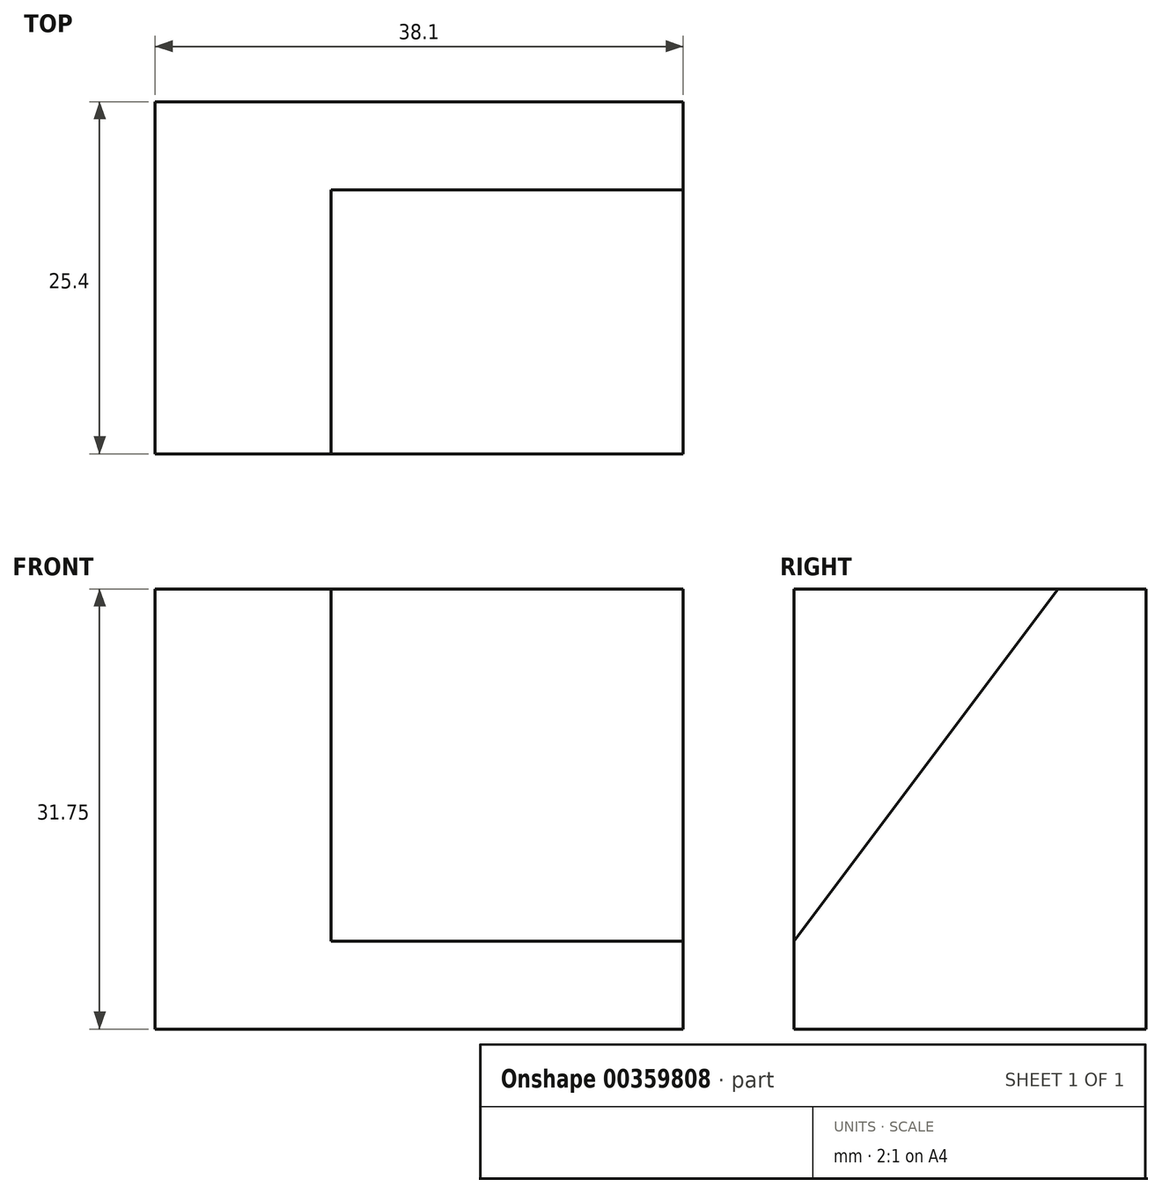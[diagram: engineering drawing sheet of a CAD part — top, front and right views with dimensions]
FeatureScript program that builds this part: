
annotation { "Feature Type Name" : "Feature", "Feature Type Description" : "" }
export const myFeature = defineFeature(function(context is Context, id is Id, definition is map)
    precondition{}
    {
        {
            var Q0;
            Q0=qCreatedBy(makeId("Front.planeOp"),FACE);
            var sketch = newSketch(context, id + "F0", { "sketchPlane" : qUnion([Q0])});
            skLineSegment(sketch, "E0.bottom", {"start": v(0, 0) * mm, "end": v(38.1, 0) * mm});
            skLineSegment(sketch, "E0.top", {"start": v(0, 31.75) * mm, "end": v(38.1, 31.75) * mm});
            skLineSegment(sketch, "E0.left", {"start": v(0, 0) * mm, "end": v(0, 31.75) * mm});
            skLineSegment(sketch, "E0.right", {"start": v(38.1, 0) * mm, "end": v(38.1, 31.75) * mm});
            skSolve(sketch);
        }
        {
            var Q0;
            Q0 = qSketchRegion(id + "F0", true);
            extrude(context, id + "F1", {"entities" : qUnion([Q0]), "depth" : 25.4 * mm});
        }
        {
            var Q0;
            Q0=makeQuery(id+"F1.opExtrude","SWEPT_FACE",FACE,{"disambiguationData":[OSD([sQuery(id+"F0.wireOp",EDGE,"E0.right")])]});
            var sketch = newSketch(context, id + "F2", { "sketchPlane" : qUnion([Q0])});
            skLineSegment(sketch, "E1", {"start": v(-6.35, 31.75) * mm, "end": v(-25.4, 6.35) * mm});
            skSolve(sketch);
        }
        {
            var Q0;
            {var subQ0=sQuery(id+"F2.wireOp",EDGE,"E1");Q0=makeQuery(id+"F2.imprint","IMPRINT",FACE,{"disambiguationData":[TD([[makeQuery(id+"F2.imprint","IMPRINT",EDGE,{"derivedFrom":subQ0}),-1.0]])]});}
            extrude(context, id + "F3", {"entities" : qUnion([Q0]), "operationType" : NewBodyOperationType.REMOVE, "oppositeDirection" : true, "depth" : 25.4 * mm});
        }
    });
